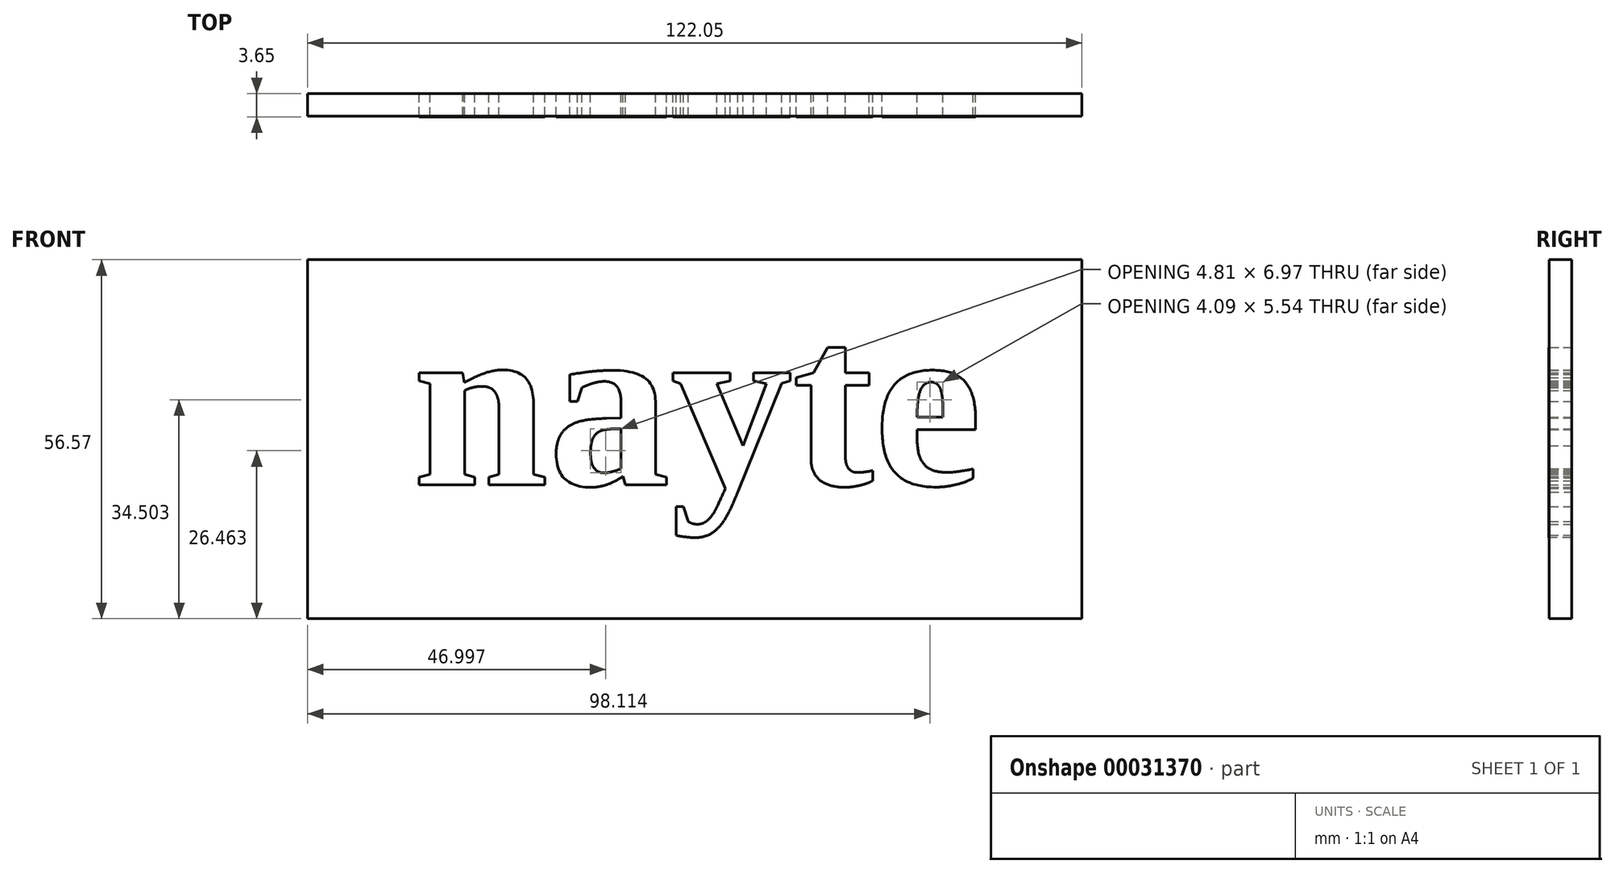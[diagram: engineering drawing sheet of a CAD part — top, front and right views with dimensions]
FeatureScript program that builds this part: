
annotation { "Feature Type Name" : "Feature", "Feature Type Description" : "" }
export const myFeature = defineFeature(function(context is Context, id is Id, definition is map)
    precondition{}
    {
        {
            var Q0;
            Q0=qCreatedBy(makeId("Front.planeOp"),FACE);
            var sketch = newSketch(context, id + "F0", { "sketchPlane" : qUnion([Q0])});
            skText(sketch, "E0", { "text": "nayte", "fontName": "Tinos-Bold.ttf"});
            const initialGuessF0  = {"E0": [-0.04438, 0.01586, 1, 0, 0.0277]};
            skSetInitialGuess(sketch, initialGuessF0);
            skSolve(sketch);
        }
        {
            var Q0;
            Q0 = qSketchRegion(id + "F0", true);
            extrude(context, id + "F1", {"entities" : qUnion([Q0]), "depth" : 3.65 * mm});
        }
        {
            var Q0;
            Q0=qCreatedBy(makeId("Front.planeOp"),FACE);
            var sketch = newSketch(context, id + "F2", { "sketchPlane" : qUnion([Q0])});
            skLineSegment(sketch, "E1.bottom", {"start": v(-60.93, 51.35) * mm, "end": v(61.12, 51.35) * mm});
            skLineSegment(sketch, "E1.top", {"start": v(-60.93, -5.22) * mm, "end": v(61.12, -5.22) * mm});
            skLineSegment(sketch, "E1.left", {"start": v(-60.93, 51.35) * mm, "end": v(-60.93, -5.22) * mm});
            skLineSegment(sketch, "E1.right", {"start": v(61.12, 51.35) * mm, "end": v(61.12, -5.22) * mm});
            skSolve(sketch);
        }
        {
            var Q0;
            Q0 = qSketchRegion(id + "F2", true);
            extrude(context, id + "F3", {"entities" : qUnion([Q0]), "depth" : 3.56 * mm});
        }
    });
